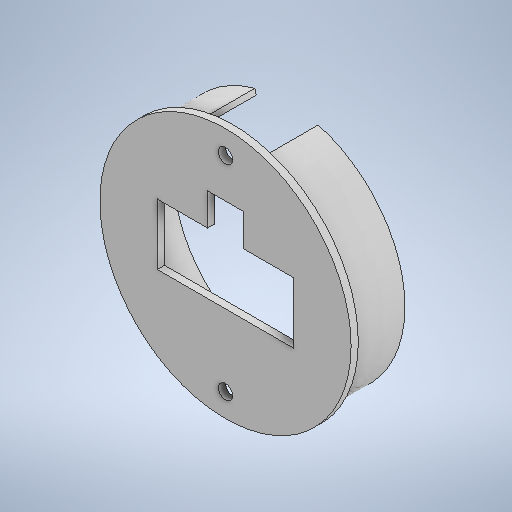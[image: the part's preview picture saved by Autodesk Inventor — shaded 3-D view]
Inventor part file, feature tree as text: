
AUTODESK INVENTOR PART (.ipt)
format: ipt  version: 2025.3 (Build 293356000, 356)  size: 269,312 bytes
history: native  units: in
note: dims shown in document units (in); Inventor stores cm internally (conversion verified against a paired STEP export)
features: reference x5, other x3, extrude x2, sketch x2, plane x1
ambient origin geometry x8: Origin, YZ Plane, XZ Plane, XY Plane, X Axis, Y Axis, Z Axis, Center Point
bodies: Solid1 (feature_tree)
feature tree (13):
  extrude  "Extrusion1"  Depth=0.5906in
  plane  "Work Plane1"
  extrude  "Extrusion2"  Depth=0.0787in TaperAngle=0.0deg
  sketch  "Sketch1"  dims[d2=0.5906in d3=0.0in d4=0.1575in]
  reference  "Reference1"
  reference  "Reference2"
  sketch  "Sketch2"  dims[d5=0.1575in d15=0.0787in d16=0.0in d36=0.0591in d37=0.0591in d38=1.9685in d39=0.9843in d40=1.4961in d41=0.6693in d44=0.3937in d45=0.4724in d46=0.2756in]
  reference  "Reference3"
  reference  "Reference4"
  reference  "Reference5"
  parser-record x1  (decoder bookkeeping rows leaked as tree rows — omitted from the tree; the rows remain in map.json)
  other  "Assembly1.iam"
  other  "main_body:1"
note: 1 file-system path scrubbed to <path> (originals preserved in map.json)
